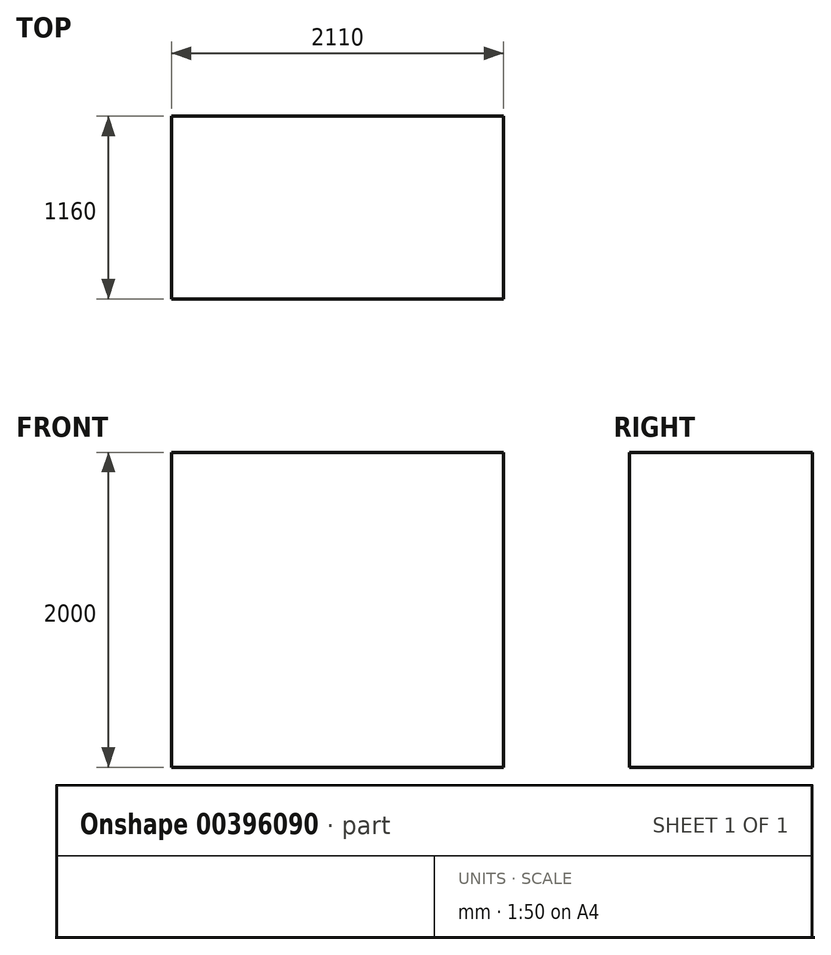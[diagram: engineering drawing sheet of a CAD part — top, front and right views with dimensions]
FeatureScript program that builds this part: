
annotation { "Feature Type Name" : "Feature", "Feature Type Description" : "" }
export const myFeature = defineFeature(function(context is Context, id is Id, definition is map)
    precondition{}
    {
        {
            var Q0;
            Q0=qCreatedBy(makeId("Top.planeOp"),FACE);
            var sketch = newSketch(context, id + "F0", { "sketchPlane" : qUnion([Q0])});
            skLineSegment(sketch, "E0.bottom", {"start": v(0, 0) * mm, "end": v(2110, 0) * mm});
            skLineSegment(sketch, "E0.top", {"start": v(0, 1160) * mm, "end": v(2110, 1160) * mm});
            skLineSegment(sketch, "E0.left", {"start": v(0, 0) * mm, "end": v(0, 1160) * mm});
            skLineSegment(sketch, "E0.right", {"start": v(2110, 0) * mm, "end": v(2110, 1160) * mm});
            skSolve(sketch);
        }
        {
            var Q0;
            Q0=makeQuery(id+"F0.imprint","IMPRINT",FACE,{"disambiguationData":[TD([[makeQuery(id+"F0.imprint","IMPRINT",EDGE,{"derivedFrom":sQuery(id+"F0.wireOp",EDGE,"E0.bottom")}),1.0]])]});
            extrude(context, id + "F1", {"entities" : qUnion([Q0]), "depth" : 2000 * mm, "offsetDistance" : 25 * mm});
        }
    });
